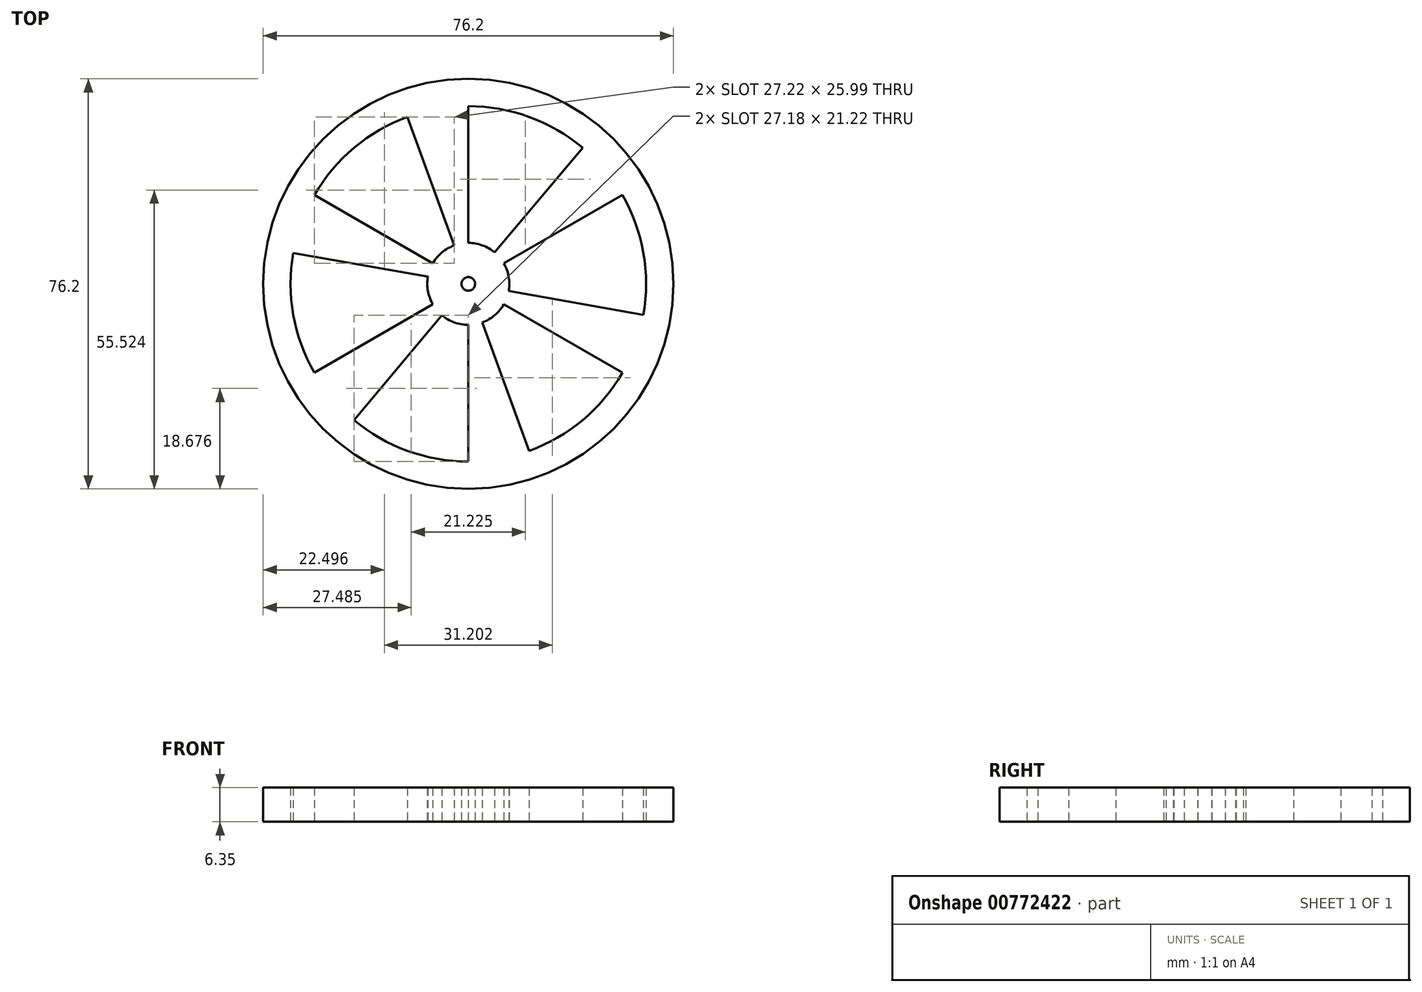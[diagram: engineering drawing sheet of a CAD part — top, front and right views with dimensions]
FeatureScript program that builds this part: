
annotation { "Feature Type Name" : "Feature", "Feature Type Description" : "" }
export const myFeature = defineFeature(function(context is Context, id is Id, definition is map)
    precondition{}
    {
        {
            var Q0;
            Q0=qCreatedBy(makeId("Top.planeOp"),FACE);
            var sketch = newSketch(context, id + "F0", { "sketchPlane" : qUnion([Q0])});
            skCircle(sketch, "E0", {"center": v(-6.82, 15.86) * mm, "radius": 38.1 * mm});
            skArc(sketch, "E1", {"start": v(14.4, 41.16) * mm, "mid": v(4.47, 46.9) * mm, "end": v(-6.82, 48.88) * mm});
            skArc(sketch, "E2", {"start": v(-1.92, 21.7) * mm, "mid": v(-4.22, 23.02) * mm, "end": v(-6.82, 23.48) * mm});
            skLineSegment(sketch, "E3", {"start": v(-6.82, 23.48) * mm, "end": v(-6.82, 48.88) * mm});
            skLineSegment(sketch, "E4", {"start": v(-1.92, 21.7) * mm, "end": v(14.4, 41.16) * mm});
            skLineSegment(sketch, "E5.1.0", {"start": v(-13.42, 19.67) * mm, "end": v(-35.42, 32.37) * mm});
            skArc(sketch, "E5.1.1", {"start": v(-18.12, 46.9) * mm, "mid": v(-28.05, 41.16) * mm, "end": v(-35.42, 32.37) * mm});
            skLineSegment(sketch, "E5.1.2", {"start": v(-9.43, 23.02) * mm, "end": v(-18.12, 46.9) * mm});
            skArc(sketch, "E5.1.3", {"start": v(-9.43, 23.02) * mm, "mid": v(-11.72, 21.7) * mm, "end": v(-13.42, 19.67) * mm});
            skLineSegment(sketch, "E5.2.0", {"start": v(-13.42, 12.05) * mm, "end": v(-35.42, -0.65) * mm});
            skArc(sketch, "E5.2.1", {"start": v(-39.34, 21.6) * mm, "mid": v(-39.34, 10.13) * mm, "end": v(-35.42, -0.65) * mm});
            skLineSegment(sketch, "E5.2.2", {"start": v(-14.33, 17.19) * mm, "end": v(-39.34, 21.6) * mm});
            skArc(sketch, "E5.2.3", {"start": v(-14.33, 17.19) * mm, "mid": v(-14.33, 14.54) * mm, "end": v(-13.42, 12.05) * mm});
            skLineSegment(sketch, "E5.3.0", {"start": v(-6.82, 8.24) * mm, "end": v(-6.82, -17.16) * mm});
            skArc(sketch, "E5.3.1", {"start": v(-28.05, -9.43) * mm, "mid": v(-18.12, -15.16) * mm, "end": v(-6.82, -17.16) * mm});
            skLineSegment(sketch, "E5.3.2", {"start": v(-11.72, 10.03) * mm, "end": v(-28.05, -9.43) * mm});
            skArc(sketch, "E5.3.3", {"start": v(-11.72, 10.03) * mm, "mid": v(-9.43, 8.7) * mm, "end": v(-6.82, 8.24) * mm});
            skLineSegment(sketch, "E5.4.0", {"start": v(-0.22, 12.05) * mm, "end": v(21.77, -0.65) * mm});
            skArc(sketch, "E5.4.1", {"start": v(4.47, -15.16) * mm, "mid": v(14.4, -9.43) * mm, "end": v(21.77, -0.65) * mm});
            skLineSegment(sketch, "E5.4.2", {"start": v(-4.22, 8.7) * mm, "end": v(4.47, -15.16) * mm});
            skArc(sketch, "E5.4.3", {"start": v(-4.22, 8.7) * mm, "mid": v(-1.92, 10.03) * mm, "end": v(-0.22, 12.05) * mm});
            skLineSegment(sketch, "E5.5.0", {"start": v(-0.22, 19.67) * mm, "end": v(21.77, 32.37) * mm});
            skArc(sketch, "E5.5.1", {"start": v(25.7, 10.13) * mm, "mid": v(25.7, 21.6) * mm, "end": v(21.77, 32.37) * mm});
            skLineSegment(sketch, "E5.5.2", {"start": v(0.68, 14.54) * mm, "end": v(25.7, 10.13) * mm});
            skArc(sketch, "E5.5.3", {"start": v(0.68, 14.54) * mm, "mid": v(0.68, 17.19) * mm, "end": v(-0.22, 19.67) * mm});
            skCircle(sketch, "E6", {"center": v(-6.82, 15.86) * mm, "radius": 1.27 * mm});
            skSolve(sketch);
        }
        {
            var Q0;
            Q0 = qSketchRegion(id + "F0", true);
            extrude(context, id + "F1", {"entities" : qUnion([Q0]), "depth" : 6.35 * mm, "offsetDistance" : 25.4 * mm});
        }
    });
